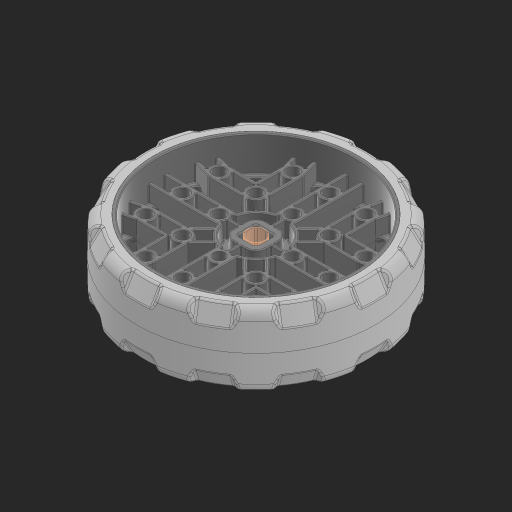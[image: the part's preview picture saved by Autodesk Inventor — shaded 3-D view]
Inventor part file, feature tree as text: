
AUTODESK INVENTOR PART (.ipt)
format: ipt  version: 2023 (Build 270158000, 158)  size: 7,971,840 bytes
history: native  units: in
note: dims shown in document units (in); Inventor stores cm internally (conversion verified against a paired STEP export)
features: other x3, sketch x1, extrude x1
ambient origin geometry x8: Origin, YZ Plane, XZ Plane, XY Plane, X Axis, Y Axis, Z Axis, Center Point
bodies: Solid1 (feature_tree), Solid2 (feature_tree)
feature tree (5):
  sketch  "Sketch1"  dims[d0=0.3937in d1=0.0in]
  other  "Srf1"
  other  "276-7771-001 Rev4_1:1"
  other  "276-7771-002 Rev4_2:1"
  extrude  "ExtrusionSrf1"  [1 undecoded]
note: 1 required parameter value undecoded (feature->parameter linkage not recoverable at this tier; creation-order binding heuristic only, values carry confidence <= 0.55)
